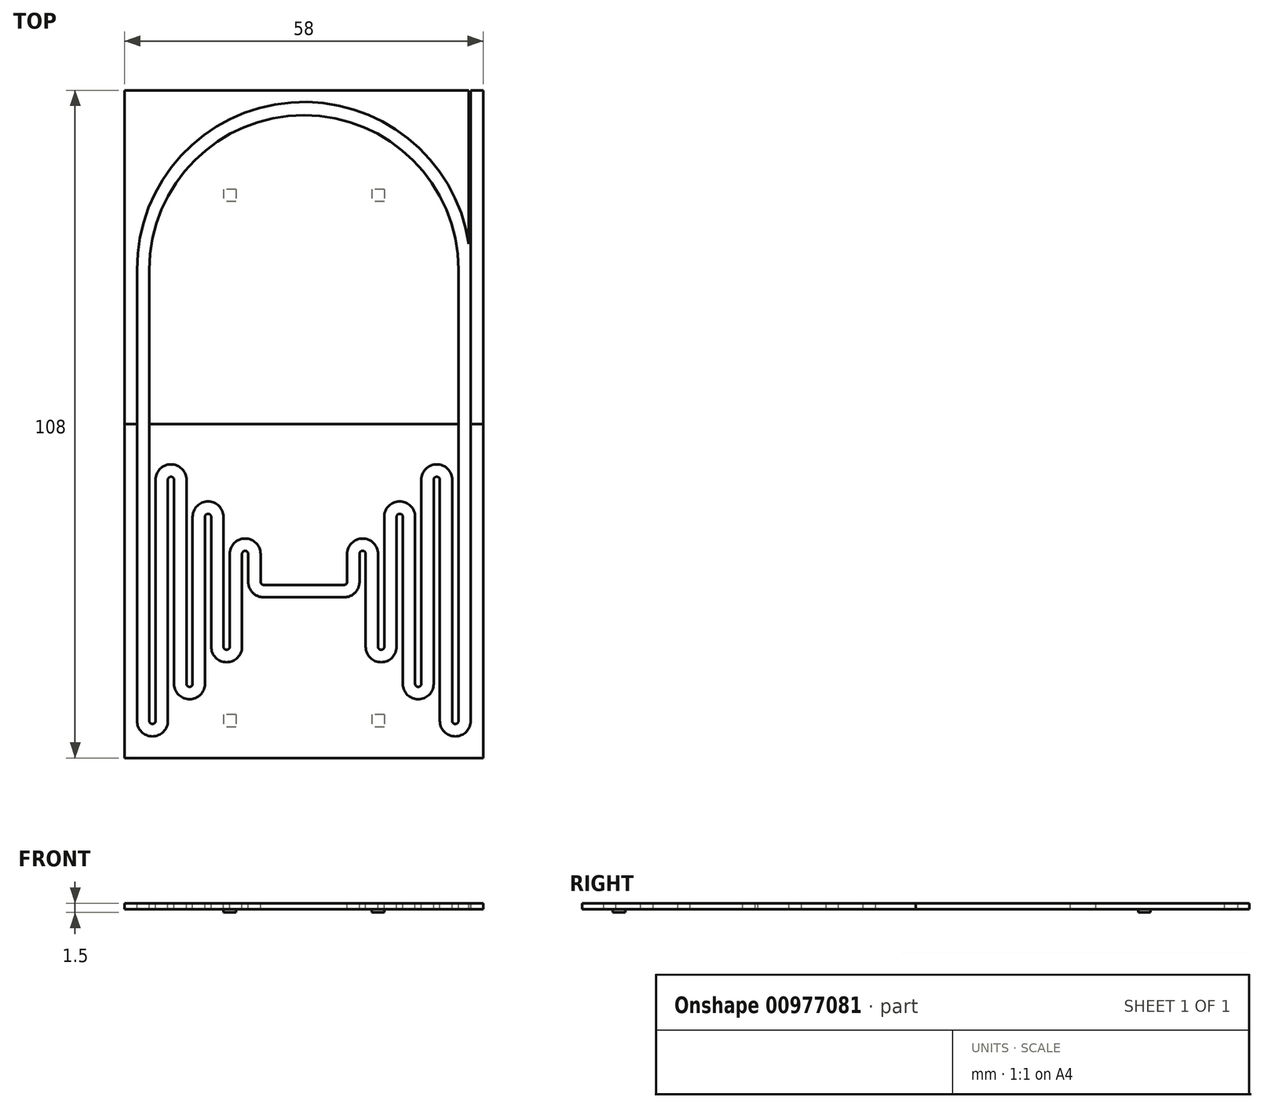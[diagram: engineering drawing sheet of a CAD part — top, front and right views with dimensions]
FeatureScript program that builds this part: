
annotation { "Feature Type Name" : "Feature", "Feature Type Description" : "" }
export const myFeature = defineFeature(function(context is Context, id is Id, definition is map)
    precondition{}
    {
        {
            var Q0;
            Q0=qCreatedBy(makeId("Top.planeOp"),FACE);
            var sketch = newSketch(context, id + "F0", { "sketchPlane" : qUnion([Q0])});
            skLineSegment(sketch, "E0.bottom", {"start": v(29, 27) * mm, "end": v(-29, 27) * mm});
            skLineSegment(sketch, "E0.top", {"start": v(29, -27) * mm, "end": v(-29, -27) * mm});
            skLineSegment(sketch, "E0.left", {"start": v(29, 27) * mm, "end": v(29, -27) * mm});
            skLineSegment(sketch, "E0.right", {"start": v(-29, 27) * mm, "end": v(-29, -27) * mm});
            skPoint(sketch, "E0.middle", {"position": v(0, 0) * mm});
            skSolve(sketch);
        }
        {
            var Q0;
            Q0=makeQuery(id+"F0.imprint","IMPRINT",FACE,{"disambiguationData":[TD([[makeQuery(id+"F0.imprint","IMPRINT",EDGE,{"derivedFrom":sQuery(id+"F0.wireOp",EDGE,"E0.bottom")}),1.0]])]});
            extrude(context, id + "F1", {"entities" : qUnion([Q0]), "depth" : 1 * mm, "offsetDistance" : 25 * mm});
        }
        {
            var Q0;
            Q0=makeQuery(id+"F1.opExtrude","CAP_FACE",FACE,{"disambiguationData":[OSD([sQuery(id+"F0.wireOp",EDGE,"E0.bottom"),sQuery(id+"F0.wireOp",EDGE,"E0.top"),sQuery(id+"F0.wireOp",EDGE,"E0.left"),sQuery(id+"F0.wireOp",EDGE,"E0.right")])],"isStart":false});
            var sketch = newSketch(context, id + "F2", { "sketchPlane" : qUnion([Q0])});
            skPoint(sketch, "E1.middle", {"position": v(-28, 0) * mm});
            skLineSegment(sketch, "E2.left", {"start": v(-27, 25) * mm, "end": v(-27, -21) * mm});
            skLineSegment(sketch, "E2.right", {"start": v(-25, 23.27) * mm, "end": v(-25, -21) * mm});
            skLineSegment(sketch, "E3.left", {"start": v(-25, 18) * mm, "end": v(-25, -21) * mm});
            skLineSegment(sketch, "E3.right", {"start": v(-24, 18) * mm, "end": v(-24, -21) * mm});
            skLineSegment(sketch, "E4.right", {"start": v(-22, 18) * mm, "end": v(-22, -21) * mm});
            skLineSegment(sketch, "E5.left", {"start": v(-21, 18) * mm, "end": v(-21, -15) * mm});
            skLineSegment(sketch, "E5.right", {"start": v(-19, 18) * mm, "end": v(-19, -15) * mm});
            skLineSegment(sketch, "E6.left", {"start": v(-18, 12) * mm, "end": v(-18, -15) * mm});
            skLineSegment(sketch, "E6.right", {"start": v(-16, 12) * mm, "end": v(-16, -15) * mm});
            skLineSegment(sketch, "E7.left", {"start": v(-15, 12) * mm, "end": v(-15, -9) * mm});
            skLineSegment(sketch, "E7.right", {"start": v(-13, 12) * mm, "end": v(-13, -9) * mm});
            skLineSegment(sketch, "E8.left", {"start": v(-12, 6) * mm, "end": v(-12, -9) * mm});
            skLineSegment(sketch, "E8.right", {"start": v(-10, 6) * mm, "end": v(-10, -9) * mm});
            skPoint(sketch, "E9.firstSnap0", {"position": v(-13, 1.5) * mm});
            skLineSegment(sketch, "E10.left", {"start": v(-9, 6) * mm, "end": v(-9, 1.5) * mm});
            skLineSegment(sketch, "E10.right", {"start": v(-7, 6) * mm, "end": v(-7, 1.5) * mm});
            skLineSegment(sketch, "E11.bottom", {"start": v(6.5, 1) * mm, "end": v(-6.5, 1) * mm});
            skLineSegment(sketch, "E11.top", {"start": v(6.5, -1) * mm, "end": v(-6.5, -1) * mm});
            skPoint(sketch, "E11.middle", {"position": v(0, 0) * mm});
            skArc(sketch, "E12", {"start": v(-9, 6) * mm, "mid": v(-9.5, 6.5) * mm, "end": v(-10, 6) * mm});
            skArc(sketch, "E13", {"start": v(-7, 6) * mm, "mid": v(-9.5, 8.5) * mm, "end": v(-12, 6) * mm});
            skArc(sketch, "E14", {"start": v(-13, -9) * mm, "mid": v(-12.5, -9.5) * mm, "end": v(-12, -9) * mm});
            skArc(sketch, "E15", {"start": v(-15, -9) * mm, "mid": v(-12.5, -11.5) * mm, "end": v(-10, -9) * mm});
            skArc(sketch, "E16", {"start": v(-15, 12) * mm, "mid": v(-15.5, 12.5) * mm, "end": v(-16, 12) * mm});
            skArc(sketch, "E17", {"start": v(-13, 12) * mm, "mid": v(-15.5, 14.5) * mm, "end": v(-18, 12) * mm});
            skArc(sketch, "E18", {"start": v(-19, -15) * mm, "mid": v(-18.5, -15.5) * mm, "end": v(-18, -15) * mm});
            skArc(sketch, "E19", {"start": v(-21, -15) * mm, "mid": v(-18.5, -17.5) * mm, "end": v(-16, -15) * mm});
            skArc(sketch, "E20", {"start": v(-21, 18) * mm, "mid": v(-21.5, 18.5) * mm, "end": v(-22, 18) * mm});
            skArc(sketch, "E21", {"start": v(-19, 18) * mm, "mid": v(-21.5, 20.5) * mm, "end": v(-24, 18) * mm});
            skArc(sketch, "E22", {"start": v(-25, -21) * mm, "mid": v(-24.5, -21.5) * mm, "end": v(-24, -21) * mm});
            skArc(sketch, "E23", {"start": v(-27, -21) * mm, "mid": v(-24.5, -23.5) * mm, "end": v(-22, -21) * mm});
            skArc(sketch, "E24", {"start": v(-7, 1.5) * mm, "mid": v(-6.86, 1.14) * mm, "end": v(-6.5, 1) * mm});
            skArc(sketch, "E25", {"start": v(-9, 1.5) * mm, "mid": v(-8.27, -0.27) * mm, "end": v(-6.5, -1) * mm});
            skLineSegment(sketch, "E26.left", {"start": v(25, 25) * mm, "end": v(25, -21) * mm});
            skLineSegment(sketch, "E26.right", {"start": v(27, 23.27) * mm, "end": v(27, -21) * mm});
            skLineSegment(sketch, "E27.right", {"start": v(25, 23.27) * mm, "end": v(25, -22.73) * mm});
            skLineSegment(sketch, "E28.left", {"start": v(22, 18) * mm, "end": v(22, -21) * mm});
            skLineSegment(sketch, "E28.right", {"start": v(24, 18) * mm, "end": v(24, -21) * mm});
            skLineSegment(sketch, "E29.left", {"start": v(19, 18) * mm, "end": v(19, -15) * mm});
            skLineSegment(sketch, "E29.right", {"start": v(21, 18) * mm, "end": v(21, -15) * mm});
            skLineSegment(sketch, "E30.left", {"start": v(16, 12) * mm, "end": v(16, -15) * mm});
            skLineSegment(sketch, "E30.right", {"start": v(18, 12) * mm, "end": v(18, -15) * mm});
            skLineSegment(sketch, "E31.right", {"start": v(16, 12) * mm, "end": v(16, -16.73) * mm});
            skLineSegment(sketch, "E32.left", {"start": v(13, 12) * mm, "end": v(13, -9) * mm});
            skLineSegment(sketch, "E32.right", {"start": v(15, 12) * mm, "end": v(15, -9) * mm});
            skLineSegment(sketch, "E33.left", {"start": v(10, 6) * mm, "end": v(10, -9) * mm});
            skLineSegment(sketch, "E33.right", {"start": v(12, 6) * mm, "end": v(12, -9) * mm});
            skLineSegment(sketch, "E34.left", {"start": v(7, 6) * mm, "end": v(7, 1.5) * mm});
            skLineSegment(sketch, "E34.right", {"start": v(9, 6) * mm, "end": v(9, 1.5) * mm});
            skArc(sketch, "E35", {"start": v(6.5, 1) * mm, "mid": v(6.85, 1.14) * mm, "end": v(7, 1.5) * mm});
            skArc(sketch, "E36", {"start": v(6.5, -1) * mm, "mid": v(8.26, -0.27) * mm, "end": v(9, 1.5) * mm});
            skArc(sketch, "E37", {"start": v(22, -21) * mm, "mid": v(24.5, -23.5) * mm, "end": v(27, -21) * mm});
            skArc(sketch, "E38", {"start": v(24, -21) * mm, "mid": v(24.5, -21.5) * mm, "end": v(25, -21) * mm});
            skArc(sketch, "E39", {"start": v(18, -15) * mm, "mid": v(18.5, -15.5) * mm, "end": v(19, -15) * mm});
            skArc(sketch, "E40", {"start": v(16, -15) * mm, "mid": v(18.5, -17.5) * mm, "end": v(21, -15) * mm});
            skArc(sketch, "E41", {"start": v(12, -9) * mm, "mid": v(12.5, -9.5) * mm, "end": v(13, -9) * mm});
            skArc(sketch, "E42", {"start": v(10, -9) * mm, "mid": v(12.5, -11.5) * mm, "end": v(15, -9) * mm});
            skArc(sketch, "E43", {"start": v(22, 18) * mm, "mid": v(21.5, 18.5) * mm, "end": v(21, 18) * mm});
            skArc(sketch, "E44", {"start": v(24, 18) * mm, "mid": v(21.5, 20.5) * mm, "end": v(19, 18) * mm});
            skArc(sketch, "E45", {"start": v(16, 12) * mm, "mid": v(15.5, 12.5) * mm, "end": v(15, 12) * mm});
            skArc(sketch, "E46", {"start": v(18, 12) * mm, "mid": v(15.5, 14.5) * mm, "end": v(13, 12) * mm});
            skArc(sketch, "E47", {"start": v(10, 6) * mm, "mid": v(9.5, 6.5) * mm, "end": v(9, 6) * mm});
            skArc(sketch, "E48", {"start": v(12, 6) * mm, "mid": v(9.5, 8.5) * mm, "end": v(7, 6) * mm});
            skLineSegment(sketch, "E49.top", {"start": v(-27, 27) * mm, "end": v(-25, 27) * mm});
            skLineSegment(sketch, "E49.left", {"start": v(-27, 25) * mm, "end": v(-27, 27) * mm});
            skLineSegment(sketch, "E49.right", {"start": v(-25, 25) * mm, "end": v(-25, 27) * mm});
            skLineSegment(sketch, "E50.top", {"start": v(25, 27) * mm, "end": v(27, 27) * mm});
            skLineSegment(sketch, "E50.left", {"start": v(25, 23.27) * mm, "end": v(25, 27) * mm});
            skLineSegment(sketch, "E50.right", {"start": v(27, 25) * mm, "end": v(27, 27) * mm});
            skLineSegment(sketch, "E51", {"start": v(27, 25) * mm, "end": v(27, 23.27) * mm});
            skLineSegment(sketch, "E52", {"start": v(-25, 25) * mm, "end": v(-25, 23.27) * mm});
            skSolve(sketch);
        }
        {
            var Q0;
            Q0=makeQuery(id+"F2.imprint","IMPRINT",FACE,{"disambiguationData":[TD([[makeQuery(id+"F2.imprint","IMPRINT",EDGE,{"derivedFrom":sQuery(id+"F2.wireOp",EDGE,"E2.left")}),1.0]])]});
            extrude(context, id + "F3", {"entities" : qUnion([Q0]), "operationType" : NewBodyOperationType.REMOVE, "oppositeDirection" : true, "depth" : 1 * mm, "offsetDistance" : 25 * mm});
        }
        {
            var Q0;
            Q0=qCreatedBy(makeId("Top.planeOp"),FACE);
            var sketch = newSketch(context, id + "F4", { "sketchPlane" : qUnion([Q0])});
            skLineSegment(sketch, "E53.bottom", {"start": v(-29, 27) * mm, "end": v(29, 27) * mm});
            skLineSegment(sketch, "E53.top", {"start": v(-29, 81) * mm, "end": v(29, 81) * mm});
            skLineSegment(sketch, "E53.left", {"start": v(-29, 27) * mm, "end": v(-29, 81) * mm});
            skLineSegment(sketch, "E53.right", {"start": v(29, 27) * mm, "end": v(29, 81) * mm});
            skSolve(sketch);
        }
        {
            var Q0;
            Q0=makeQuery(id+"F4.imprint","IMPRINT",FACE,{"disambiguationData":[TD([[makeQuery(id+"F4.imprint","IMPRINT",EDGE,{"derivedFrom":sQuery(id+"F4.wireOp",EDGE,"E53.bottom")}),1.0]])]});
            extrude(context, id + "F5", {"entities" : qUnion([Q0]), "depth" : 1 * mm, "offsetDistance" : 25 * mm});
        }
        {
            var Q0;
            Q0=makeQuery(id+"F5.opExtrude","CAP_FACE",FACE,{"disambiguationData":[OSD([sQuery(id+"F4.wireOp",EDGE,"E53.bottom"),sQuery(id+"F4.wireOp",EDGE,"E53.top"),sQuery(id+"F4.wireOp",EDGE,"E53.left"),sQuery(id+"F4.wireOp",EDGE,"E53.right")])],"isStart":false});
            var sketch = newSketch(context, id + "F6", { "sketchPlane" : qUnion([Q0])});
            skLineSegment(sketch, "E54.bottom", {"start": v(-27, 27) * mm, "end": v(-25, 27) * mm});
            skLineSegment(sketch, "E54.top", {"start": v(-27, 52) * mm, "end": v(-25, 52) * mm});
            skLineSegment(sketch, "E54.left", {"start": v(-27, 27) * mm, "end": v(-27, 52) * mm});
            skLineSegment(sketch, "E54.right", {"start": v(-25, 27) * mm, "end": v(-25, 52) * mm});
            skLineSegment(sketch, "E55.bottom", {"start": v(27, 27) * mm, "end": v(25, 27) * mm});
            skLineSegment(sketch, "E55.top", {"start": v(27, 52) * mm, "end": v(25, 52) * mm});
            skLineSegment(sketch, "E55.left", {"start": v(27, 27) * mm, "end": v(27, 52) * mm});
            skLineSegment(sketch, "E55.right", {"start": v(25, 27) * mm, "end": v(25, 52) * mm});
            skArc(sketch, "E56", {"start": v(25, 52) * mm, "mid": v(0, 77) * mm, "end": v(-25, 52) * mm});
            skArc(sketch, "E57", {"start": v(27, 52) * mm, "mid": v(0, 79.13) * mm, "end": v(-27, 52) * mm});
            skPoint(sketch, "E57.startSnap0", {"position": v(27, 39.5) * mm});
            skLineSegment(sketch, "E58.bottom", {"start": v(27, 52) * mm, "end": v(26.7, 52) * mm});
            skLineSegment(sketch, "E58.top", {"start": v(27, 81) * mm, "end": v(26.7, 81) * mm});
            skLineSegment(sketch, "E58.left", {"start": v(27, 52) * mm, "end": v(27, 81) * mm});
            skLineSegment(sketch, "E58.right", {"start": v(26.7, 52) * mm, "end": v(26.7, 81) * mm});
            skSolve(sketch);
        }
        {
            var Q0;
            Q0=qSketchRegion(id+"F6",true);
            extrude(context, id + "F7", {"entities" : qUnion([Q0]), "operationType" : NewBodyOperationType.REMOVE, "oppositeDirection" : true, "depth" : 1 * mm, "offsetDistance" : 25 * mm});
        }
        {
            var Q0;
            {var subQ0=sQuery(id+"F0.wireOp",EDGE,"E0.left");var subQ1=sQuery(id+"F0.wireOp",EDGE,"E0.top");var subQ2=sQuery(id+"F0.wireOp",EDGE,"E0.right");var subQ3=sQuery(id+"F0.wireOp",EDGE,"E0.bottom");Q0=makeQuery(id+"F3.boolean.opBoolean","SPLIT",FACE,{"disambiguationData":[TD([makeQuery(id+"F1.opExtrude","SWEPT_FACE",FACE,{"disambiguationData":[OSD([subQ1])]})])],"derivedFrom":makeQuery(id+"F1.opExtrude","CAP_FACE",FACE,{"disambiguationData":[OSD([subQ3,subQ1,subQ0,subQ2])],"isStart":true})});}
            var sketch = newSketch(context, id + "F8", { "sketchPlane" : qUnion([Q0])});
            skLineSegment(sketch, "E59.bottom", {"start": v(13, 20) * mm, "end": v(11, 20) * mm});
            skLineSegment(sketch, "E59.top", {"start": v(13, 22) * mm, "end": v(11, 22) * mm});
            skLineSegment(sketch, "E59.left", {"start": v(13, 20) * mm, "end": v(13, 22) * mm});
            skLineSegment(sketch, "E59.right", {"start": v(11, 20) * mm, "end": v(11, 22) * mm});
            skLineSegment(sketch, "E60.bottom", {"start": v(-11, 20) * mm, "end": v(-13, 20) * mm});
            skLineSegment(sketch, "E60.top", {"start": v(-11, 22) * mm, "end": v(-13, 22) * mm});
            skLineSegment(sketch, "E60.left", {"start": v(-11, 20) * mm, "end": v(-11, 22) * mm});
            skLineSegment(sketch, "E60.right", {"start": v(-13, 20) * mm, "end": v(-13, 22) * mm});
            skSolve(sketch);
        }
        {
            var Q0;
            Q0=makeQuery(id+"F8.imprint","IMPRINT",FACE,{"disambiguationData":[TD([[makeQuery(id+"F8.imprint","IMPRINT",EDGE,{"derivedFrom":sQuery(id+"F8.wireOp",EDGE,"E59.bottom")}),-1.0]])]});
            var Q1;
            Q1=makeQuery(id+"F8.imprint","IMPRINT",FACE,{"disambiguationData":[TD([[makeQuery(id+"F8.imprint","IMPRINT",EDGE,{"derivedFrom":sQuery(id+"F8.wireOp",EDGE,"E60.bottom")}),-1.0]])]});
            extrude(context, id + "F9", {"entities" : qUnion([Q0, Q1]), "operationType" : NewBodyOperationType.ADD, "depth" : 0.5 * mm, "offsetDistance" : 25 * mm});
        }
        {
            var Q0;
            {var subQ0=sQuery(id+"F4.wireOp",EDGE,"E53.bottom");Q0=makeQuery(id+"F7.boolean.opBoolean","SPLIT",FACE,{"disambiguationData":[TD([makeQuery(id+"F7.opExtrude","SWEPT_FACE",FACE,{"disambiguationData":[OSD([sQuery(id+"F6.wireOp",EDGE,"E55.top")])]})])],"derivedFrom":makeQuery(id+"F5.opExtrude","CAP_FACE",FACE,{"disambiguationData":[OSD([subQ0,sQuery(id+"F4.wireOp",EDGE,"E53.top"),sQuery(id+"F4.wireOp",EDGE,"E53.left"),sQuery(id+"F4.wireOp",EDGE,"E53.right")])],"isStart":true})});}
            var sketch = newSketch(context, id + "F10", { "sketchPlane" : qUnion([Q0])});
            skLineSegment(sketch, "E61.bottom", {"start": v(13, -65) * mm, "end": v(11, -65) * mm});
            skLineSegment(sketch, "E61.top", {"start": v(13, -63) * mm, "end": v(11, -63) * mm});
            skLineSegment(sketch, "E61.left", {"start": v(13, -65) * mm, "end": v(13, -63) * mm});
            skLineSegment(sketch, "E61.right", {"start": v(11, -65) * mm, "end": v(11, -63) * mm});
            skLineSegment(sketch, "E62.bottom", {"start": v(-11, -65) * mm, "end": v(-13, -65) * mm});
            skLineSegment(sketch, "E62.top", {"start": v(-11, -63) * mm, "end": v(-13, -63) * mm});
            skLineSegment(sketch, "E62.left", {"start": v(-11, -65) * mm, "end": v(-11, -63) * mm});
            skLineSegment(sketch, "E62.right", {"start": v(-13, -65) * mm, "end": v(-13, -63) * mm});
            skSolve(sketch);
        }
        {
            var Q0;
            Q0=makeQuery(id+"F10.imprint","IMPRINT",FACE,{"disambiguationData":[TD([[makeQuery(id+"F10.imprint","IMPRINT",EDGE,{"derivedFrom":sQuery(id+"F10.wireOp",EDGE,"E61.bottom")}),-1.0]])]});
            var Q1;
            Q1=makeQuery(id+"F10.imprint","IMPRINT",FACE,{"disambiguationData":[TD([[makeQuery(id+"F10.imprint","IMPRINT",EDGE,{"derivedFrom":sQuery(id+"F10.wireOp",EDGE,"E62.bottom")}),-1.0]])]});
            extrude(context, id + "F11", {"entities" : qUnion([Q0, Q1]), "operationType" : NewBodyOperationType.ADD, "depth" : 0.5 * mm, "offsetDistance" : 25 * mm});
        }
    });
